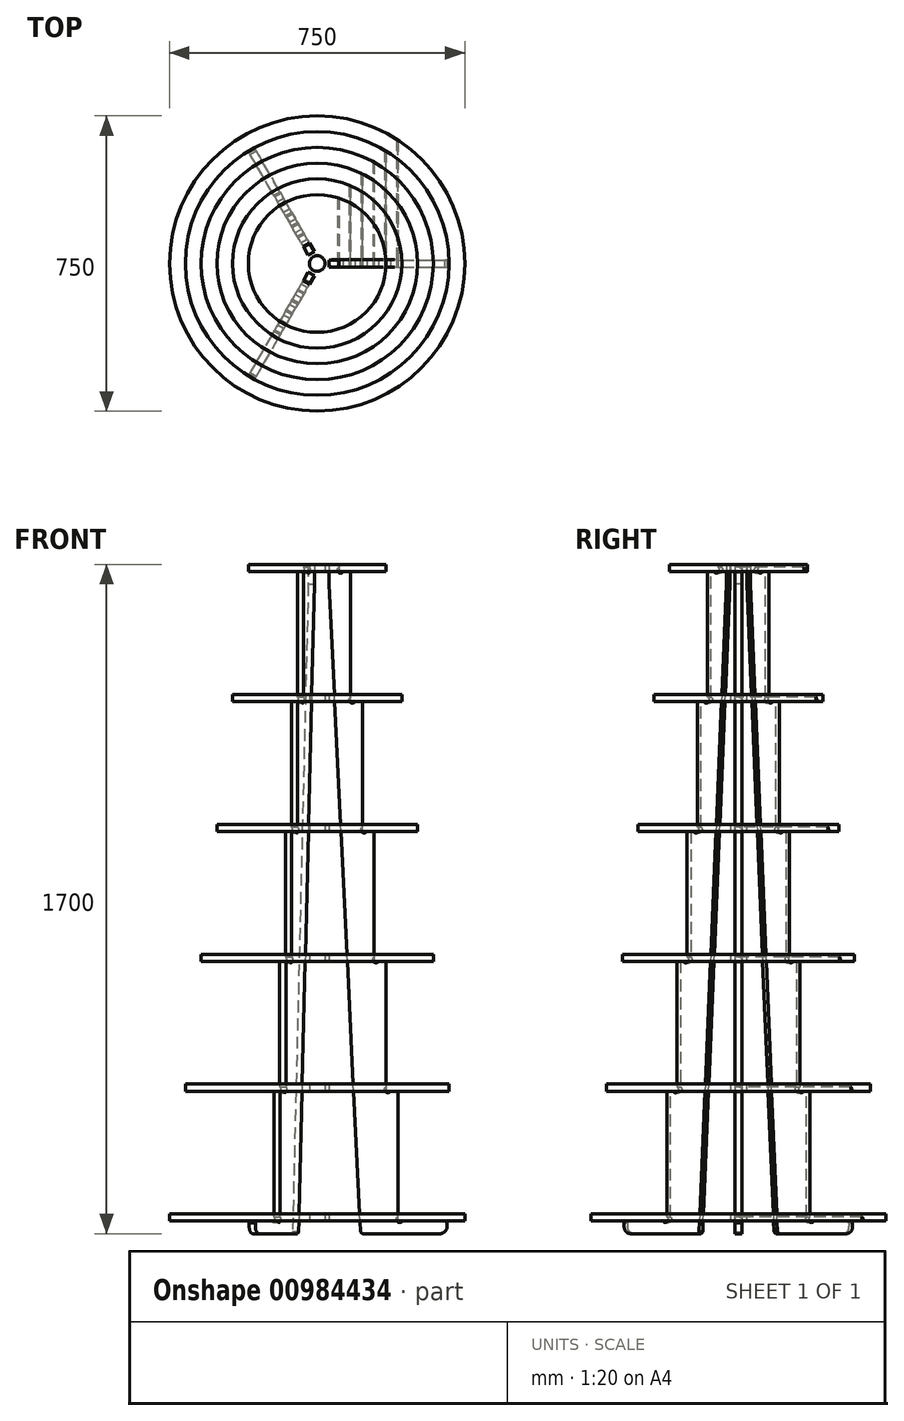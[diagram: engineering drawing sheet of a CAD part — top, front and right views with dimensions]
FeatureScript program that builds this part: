
annotation { "Feature Type Name" : "Feature", "Feature Type Description" : "" }
export const myFeature = defineFeature(function(context is Context, id is Id, definition is map)
    precondition{}
    {
        {
            var Q0;
            Q0=qCreatedBy(makeId("Top.planeOp"),FACE);
            cPlane(context, id + "F0", {"entities" : qUnion([Q0]), "cplaneType" : CPlaneType.OFFSET, "offset" : 50 * mm, "width" : 150 * mm, "height" : 150 * mm});
        }
        {
            var Q0;
            Q0=qCreatedBy(makeId("Top.planeOp"),FACE);
            cPlane(context, id + "F1", {"entities" : qUnion([Q0]), "cplaneType" : CPlaneType.OFFSET, "offset" : 1700 * mm, "width" : 150 * mm, "height" : 150 * mm});
        }
        {
            var Q0;
            Q0=qCreatedBy(id+"F0.planeOp",FACE);
            cPlane(context, id + "F2", {"entities" : qUnion([Q0]), "cplaneType" : CPlaneType.OFFSET, "offset" : (1650 / 5) * mm, "width" : 150 * mm, "height" : 150 * mm});
        }
        {
            var Q0;
            Q0=qCreatedBy(id+"F2.planeOp",FACE);
            cPlane(context, id + "F3", {"entities" : qUnion([Q0]), "cplaneType" : CPlaneType.OFFSET, "offset" : (1650 / 5) * mm, "width" : 150 * mm, "height" : 150 * mm});
        }
        {
            var Q0;
            Q0=qCreatedBy(id+"F3.planeOp",FACE);
            cPlane(context, id + "F4", {"entities" : qUnion([Q0]), "cplaneType" : CPlaneType.OFFSET, "offset" : (1650 / 5) * mm, "width" : 150 * mm, "height" : 150 * mm});
        }
        {
            var Q0;
            Q0=qCreatedBy(id+"F4.planeOp",FACE);
            cPlane(context, id + "F5", {"entities" : qUnion([Q0]), "cplaneType" : CPlaneType.OFFSET, "offset" : (1650 / 5) * mm, "width" : 150 * mm, "height" : 150 * mm});
        }
        {
            var Q0;
            Q0=qCreatedBy(id+"F0.planeOp",FACE);
            var sketch = newSketch(context, id + "F6", { "sketchPlane" : qUnion([Q0])});
            skCircle(sketch, "E0", {"center": v(0, 0) * mm, "radius": 375 * mm});
            skSolve(sketch);
        }
        {
            var Q0;
            Q0=qCreatedBy(id+"F1.planeOp",FACE);
            var sketch = newSketch(context, id + "F7", { "sketchPlane" : qUnion([Q0])});
            skCircle(sketch, "E1", {"center": v(0, 0) * mm, "radius": 175 * mm});
            skSolve(sketch);
        }
        {
            var Q0;
            Q0=qCreatedBy(makeId("Front.planeOp"),FACE);
            var sketch = newSketch(context, id + "F8", { "sketchPlane" : qUnion([Q0])});
            skLineSegment(sketch, "E2", {"start": v(375, 50) * mm, "end": v(175, 1700) * mm, "construction": true});
            skLineSegment(sketch, "E3.0", {"start": v(-175, 1700) * mm, "end": v(175, 1700) * mm, "construction": true});
            skLineSegment(sketch, "E4.0", {"start": v(-375, 50) * mm, "end": v(375, 50) * mm, "construction": true});
            skLineSegment(sketch, "E5", {"start": v(0, 380) * mm, "end": v(335, 380) * mm});
            skLineSegment(sketch, "E6", {"start": v(0, 710) * mm, "end": v(295, 710) * mm});
            skLineSegment(sketch, "E7", {"start": v(0, 1040) * mm, "end": v(255, 1040) * mm});
            skLineSegment(sketch, "E8", {"start": v(0, 1370) * mm, "end": v(215, 1370) * mm});
            skSolve(sketch);
        }
        {
            var Q0;
            Q0=qCreatedBy(id+"F2.planeOp",FACE);
            var sketch = newSketch(context, id + "F9", { "sketchPlane" : qUnion([Q0])});
            skCircle(sketch, "E9", {"center": v(0, 0) * mm, "radius": 335 * mm});
            skPoint(sketch, "E10.0", {"position": v(335, 0) * mm});
            skSolve(sketch);
        }
        {
            var Q0;
            Q0=qCreatedBy(id+"F3.planeOp",FACE);
            var sketch = newSketch(context, id + "F10", { "sketchPlane" : qUnion([Q0])});
            skPoint(sketch, "E11.0", {"position": v(295, 0) * mm});
            skCircle(sketch, "E12", {"center": v(0, 0) * mm, "radius": 295 * mm});
            skSolve(sketch);
        }
        {
            var Q0;
            Q0=qCreatedBy(id+"F4.planeOp",FACE);
            var sketch = newSketch(context, id + "F11", { "sketchPlane" : qUnion([Q0])});
            skPoint(sketch, "E13.0", {"position": v(255, 0) * mm});
            skCircle(sketch, "E14", {"center": v(0, 0) * mm, "radius": 255 * mm});
            skSolve(sketch);
        }
        {
            var Q0;
            Q0=qCreatedBy(id+"F5.planeOp",FACE);
            var sketch = newSketch(context, id + "F12", { "sketchPlane" : qUnion([Q0])});
            skPoint(sketch, "E15.0", {"position": v(215, 0) * mm});
            skCircle(sketch, "E16", {"center": v(0, 0) * mm, "radius": 215 * mm});
            skSolve(sketch);
        }
        {
            var Q0;
            Q0=qCreatedBy(makeId("Front.planeOp"),FACE);
            var sketch = newSketch(context, id + "F13", { "sketchPlane" : qUnion([Q0])});
            skLineSegment(sketch, "E17", {"start": v(0, 0) * mm, "end": v(330, 0) * mm});
            skLineSegment(sketch, "E18", {"start": v(205, 32) * mm, "end": v(205, 362) * mm});
            skLineSegment(sketch, "E19", {"start": v(205, 362) * mm, "end": v(175, 362) * mm});
            skLineSegment(sketch, "E20", {"start": v(145, 1022) * mm, "end": v(115, 1022) * mm});
            skLineSegment(sketch, "E21", {"start": v(115, 1022) * mm, "end": v(115, 1352) * mm});
            skLineSegment(sketch, "E22", {"start": v(30, 1700) * mm, "end": v(55, 1700) * mm});
            skLineSegment(sketch, "E23", {"start": v(55, 1700) * mm, "end": v(55, 1682) * mm});
            skLineSegment(sketch, "E24", {"start": v(85, 1352) * mm, "end": v(115, 1352) * mm});
            skLineSegment(sketch, "E25", {"start": v(55, 1682) * mm, "end": v(85, 1682) * mm});
            skLineSegment(sketch, "E26", {"start": v(85, 1352) * mm, "end": v(85, 1682) * mm});
            skLineSegment(sketch, "E27", {"start": v(145, 1022) * mm, "end": v(145, 692) * mm});
            skLineSegment(sketch, "E28", {"start": v(145, 692) * mm, "end": v(175, 692) * mm});
            skLineSegment(sketch, "E29", {"start": v(175, 692) * mm, "end": v(175, 362) * mm});
            skLineSegment(sketch, "E30", {"start": v(205, 32) * mm, "end": v(330, 32) * mm});
            skLineSegment(sketch, "E31", {"start": v(330, 32) * mm, "end": v(330, 0) * mm});
            skPoint(sketch, "E32.orphan", {"position": v(-14.84, 1022) * mm});
            skPoint(sketch, "E33.orphan", {"position": v(30, 0) * mm});
            skLineSegment(sketch, "E34", {"start": v(0, 0) * mm, "end": v(0, 2212.38) * mm, "construction": true});
            skLineSegment(sketch, "E35", {"start": v(30, 1700) * mm, "end": v(30, 0) * mm});
            skSolve(sketch);
        }
        {
            var Q0;
            Q0=makeQuery(id+"F7.imprint","IMPRINT",FACE,{"disambiguationData":[TD([[makeQuery(id+"F7.imprint","IMPRINT",EDGE,{"derivedFrom":sQuery(id+"F7.wireOp",EDGE,"E1")}),1.0]])]});
            var Q1;
            Q1=makeQuery(id+"F12.imprint","IMPRINT",FACE,{"disambiguationData":[TD([[makeQuery(id+"F12.imprint","IMPRINT",EDGE,{"derivedFrom":sQuery(id+"F12.wireOp",EDGE,"E16")}),1.0]])]});
            var Q2;
            Q2=makeQuery(id+"F11.imprint","IMPRINT",FACE,{"disambiguationData":[TD([[makeQuery(id+"F11.imprint","IMPRINT",EDGE,{"derivedFrom":sQuery(id+"F11.wireOp",EDGE,"E14")}),1.0]])]});
            var Q3;
            Q3=makeQuery(id+"F10.imprint","IMPRINT",FACE,{"disambiguationData":[TD([[makeQuery(id+"F10.imprint","IMPRINT",EDGE,{"derivedFrom":sQuery(id+"F10.wireOp",EDGE,"E12")}),1.0]])]});
            var Q4;
            Q4=makeQuery(id+"F9.imprint","IMPRINT",FACE,{"disambiguationData":[TD([[makeQuery(id+"F9.imprint","IMPRINT",EDGE,{"derivedFrom":sQuery(id+"F9.wireOp",EDGE,"E9")}),1.0]])]});
            var Q5;
            Q5=makeQuery(id+"F6.imprint","IMPRINT",FACE,{"disambiguationData":[TD([[makeQuery(id+"F6.imprint","IMPRINT",EDGE,{"derivedFrom":sQuery(id+"F6.wireOp",EDGE,"E0")}),1.0]])]});
            extrude(context, id + "F14", {"entities" : qUnion([Q0, Q1, Q2, Q3, Q4, Q5]), "oppositeDirection" : true, "depth" : 18 * mm, "offsetDistance" : 25 * mm});
        }
        {
            var Q0;
            Q0=makeQuery(id+"F13.imprint","IMPRINT",FACE,{"disambiguationData":[TD([[makeQuery(id+"F13.imprint","IMPRINT",EDGE,{"derivedFrom":sQuery(id+"F13.wireOp",EDGE,"E18")}),1.0]])]});
            extrude(context, id + "F15", {"entities" : qUnion([Q0]), "operationType" : NewBodyOperationType.REMOVE, "endBound" : BoundingType.SYMMETRIC, "depth" : 18.5 * mm, "offsetDistance" : 25 * mm});
        }
        {
            var Q0;
            Q0=makeQuery(id+"F13.imprint","IMPRINT",FACE,{"disambiguationData":[TD([[makeQuery(id+"F13.imprint","IMPRINT",EDGE,{"derivedFrom":sQuery(id+"F13.wireOp",EDGE,"E18")}),1.0]])]});
            extrude(context, id + "F16", {"entities" : qUnion([Q0]), "endBound" : BoundingType.SYMMETRIC, "depth" : 18 * mm, "offsetDistance" : 25 * mm});
        }
        {
            var Q0;
            Q0=makeQuery(id+"F16.opExtrude","SWEPT_EDGE",EDGE,{"disambiguationData":[OSD([sQuery(id+"F13.wireOp",EDGE,"E17"),sQuery(id+"F13.wireOp",EDGE,"E35")])]});
            chamfer(context, id + "F17", {"entities" : qUnion([Q0]), "chamferType" : ChamferType.TWO_OFFSETS, "width1" : 80 * mm, "oppositeDirection" : false, "width2" : 1650 * mm, "tangentPropagation" : true});
        }
        {
            var Q0;
            Q0=makeQuery(id+"F16.opExtrude","CAP_FACE",FACE,{"disambiguationData":[OSD([sQuery(id+"F13.wireOp",EDGE,"E17"),sQuery(id+"F13.wireOp",EDGE,"E18"),sQuery(id+"F13.wireOp",EDGE,"E19"),sQuery(id+"F13.wireOp",EDGE,"E20"),sQuery(id+"F13.wireOp",EDGE,"E21"),sQuery(id+"F13.wireOp",EDGE,"E22"),sQuery(id+"F13.wireOp",EDGE,"E23"),sQuery(id+"F13.wireOp",EDGE,"E24"),sQuery(id+"F13.wireOp",EDGE,"E25"),sQuery(id+"F13.wireOp",EDGE,"E26"),sQuery(id+"F13.wireOp",EDGE,"E27"),sQuery(id+"F13.wireOp",EDGE,"E28"),sQuery(id+"F13.wireOp",EDGE,"E29"),sQuery(id+"F13.wireOp",EDGE,"E30"),sQuery(id+"F13.wireOp",EDGE,"E31"),sQuery(id+"F13.wireOp",EDGE,"E35")])],"isStart":false});
            var sketch = newSketch(context, id + "F18", { "sketchPlane" : qUnion([Q0])});
            skArc(sketch, "E36", {"start": v(85, 1363.17) * mm, "mid": v(83.59, 1350.59) * mm, "end": v(96.17, 1352) * mm});
            skLineSegment(sketch, "E37", {"start": v(89.31, 1356.31) * mm, "end": v(85, 1352) * mm, "construction": true});
            skLineSegment(sketch, "E38", {"start": v(85, 1352) * mm, "end": v(85, 1363.17) * mm});
            skLineSegment(sketch, "E39", {"start": v(85, 1352) * mm, "end": v(96.17, 1352) * mm});
            skLineSegment(sketch, "E40", {"start": v(85, 1352) * mm, "end": v(83.59, 1350.59) * mm, "construction": true});
            skArc(sketch, "E41", {"start": v(145, 703.17) * mm, "mid": v(143.59, 690.59) * mm, "end": v(156.17, 692) * mm});
            skLineSegment(sketch, "E42", {"start": v(149.31, 696.31) * mm, "end": v(145, 692) * mm, "construction": true});
            skLineSegment(sketch, "E43", {"start": v(145, 692) * mm, "end": v(145, 703.17) * mm});
            skLineSegment(sketch, "E44", {"start": v(145, 692) * mm, "end": v(156.17, 692) * mm});
            skLineSegment(sketch, "E45", {"start": v(145, 692) * mm, "end": v(143.59, 690.59) * mm, "construction": true});
            skArc(sketch, "E46", {"start": v(205, 43.17) * mm, "mid": v(203.59, 30.59) * mm, "end": v(216.17, 32) * mm});
            skLineSegment(sketch, "E47", {"start": v(209.31, 36.31) * mm, "end": v(205, 32) * mm, "construction": true});
            skLineSegment(sketch, "E48", {"start": v(205, 32) * mm, "end": v(205, 43.17) * mm});
            skLineSegment(sketch, "E49", {"start": v(205, 32) * mm, "end": v(216.17, 32) * mm});
            skLineSegment(sketch, "E50", {"start": v(205, 32) * mm, "end": v(203.59, 30.59) * mm, "construction": true});
            skArc(sketch, "E51", {"start": v(175, 373.17) * mm, "mid": v(173.59, 360.59) * mm, "end": v(186.17, 362) * mm});
            skLineSegment(sketch, "E52", {"start": v(179.31, 366.31) * mm, "end": v(175, 362) * mm, "construction": true});
            skLineSegment(sketch, "E53", {"start": v(175, 362) * mm, "end": v(175, 373.17) * mm});
            skLineSegment(sketch, "E54", {"start": v(175, 362) * mm, "end": v(186.17, 362) * mm});
            skLineSegment(sketch, "E55", {"start": v(175, 362) * mm, "end": v(173.59, 360.59) * mm, "construction": true});
            skArc(sketch, "E56", {"start": v(55, 1693.17) * mm, "mid": v(53.59, 1680.59) * mm, "end": v(66.17, 1682) * mm});
            skLineSegment(sketch, "E57", {"start": v(59.31, 1686.31) * mm, "end": v(55, 1682) * mm, "construction": true});
            skLineSegment(sketch, "E58", {"start": v(55, 1682) * mm, "end": v(55, 1693.17) * mm});
            skLineSegment(sketch, "E59", {"start": v(55, 1682) * mm, "end": v(66.17, 1682) * mm});
            skLineSegment(sketch, "E60", {"start": v(55, 1682) * mm, "end": v(53.59, 1680.59) * mm, "construction": true});
            skArc(sketch, "E61", {"start": v(115, 1033.17) * mm, "mid": v(113.59, 1020.59) * mm, "end": v(126.17, 1022) * mm});
            skLineSegment(sketch, "E62", {"start": v(119.31, 1026.31) * mm, "end": v(115, 1022) * mm, "construction": true});
            skLineSegment(sketch, "E63", {"start": v(115, 1022) * mm, "end": v(115, 1033.17) * mm});
            skLineSegment(sketch, "E64", {"start": v(115, 1022) * mm, "end": v(126.17, 1022) * mm});
            skLineSegment(sketch, "E65", {"start": v(115, 1022) * mm, "end": v(113.59, 1020.59) * mm, "construction": true});
            skSolve(sketch);
        }
        {
            var Q0;
            Q0=makeQuery(id+"F18.imprint","IMPRINT",FACE,{"disambiguationData":[TD([[makeQuery(id+"F18.imprint","IMPRINT",EDGE,{"derivedFrom":sQuery(id+"F18.wireOp",EDGE,"E46")}),1.0]])]});
            var Q1;
            Q1=makeQuery(id+"F18.imprint","IMPRINT",FACE,{"disambiguationData":[TD([[makeQuery(id+"F18.imprint","IMPRINT",EDGE,{"derivedFrom":sQuery(id+"F18.wireOp",EDGE,"E51")}),1.0]])]});
            var Q2;
            Q2=makeQuery(id+"F18.imprint","IMPRINT",FACE,{"disambiguationData":[TD([[makeQuery(id+"F18.imprint","IMPRINT",EDGE,{"derivedFrom":sQuery(id+"F18.wireOp",EDGE,"E41")}),1.0]])]});
            var Q3;
            Q3=makeQuery(id+"F18.imprint","IMPRINT",FACE,{"disambiguationData":[TD([[makeQuery(id+"F18.imprint","IMPRINT",EDGE,{"derivedFrom":sQuery(id+"F18.wireOp",EDGE,"E61")}),1.0]])]});
            var Q4;
            Q4=makeQuery(id+"F18.imprint","IMPRINT",FACE,{"disambiguationData":[TD([[makeQuery(id+"F18.imprint","IMPRINT",EDGE,{"derivedFrom":sQuery(id+"F18.wireOp",EDGE,"E36")}),1.0]])]});
            var Q5;
            Q5=makeQuery(id+"F18.imprint","IMPRINT",FACE,{"disambiguationData":[TD([[makeQuery(id+"F18.imprint","IMPRINT",EDGE,{"derivedFrom":sQuery(id+"F18.wireOp",EDGE,"E56")}),1.0]])]});
            extrude(context, id + "F19", {"entities" : qUnion([Q0, Q1, Q2, Q3, Q4, Q5]), "operationType" : NewBodyOperationType.REMOVE, "endBound" : BoundingType.THROUGH_ALL, "oppositeDirection" : true, "depth" : 25 * mm, "offsetDistance" : 25 * mm});
        }
        {
            var Q0;
            Q0=makeQuery(id+"F16.opExtrude","SWEPT_EDGE",EDGE,{"disambiguationData":[OSD([sQuery(id+"F13.wireOp",EDGE,"E17"),sQuery(id+"F13.wireOp",EDGE,"E31")])]});
            fillet(context, id + "F20", {"entities" : qUnion([Q0]), "radius" : 18 * mm, "tangentPropagation" : true, "allowEdgeOverflow" : false});
        }
        {
            var Q0;
            Q0=makeQuery(id+"F16.opExtrude","SWEPT_EDGE",EDGE,{"disambiguationData":[OSD([sQuery(id+"F13.wireOp",EDGE,"E30"),sQuery(id+"F13.wireOp",EDGE,"E31")])]});
            var Q1;
            {var subQ0=sQuery(id+"F13.wireOp",EDGE,"E17");Q1=makeQuery(id+"F17.opChamfer","BLEND_EDGE",EDGE,{"blendedFrom":[makeQuery(id+"F16.opExtrude","SWEPT_EDGE",EDGE,{"disambiguationData":[OSD([subQ0,sQuery(id+"F13.wireOp",EDGE,"E35")])]}),makeQuery(id+"F16.opExtrude","SWEPT_FACE",FACE,{"disambiguationData":[OSD([subQ0])]})],"blendedInto":[makeQuery(id+"F16.opExtrude","SWEPT_FACE",FACE,{"disambiguationData":[OSD([subQ0])]})]});}
            chamfer(context, id + "F21", {"entities" : qUnion([Q0, Q1]), "width" : 5 * mm, "tangentPropagation" : true});
        }
        {
            var Q0;
            Q0=makeQuery(id+"F16.opExtrude","SWEPT_BODY",BODY,{"disambiguationData":[OSD([sQuery(id+"F13.wireOp",EDGE,"E17"),sQuery(id+"F13.wireOp",EDGE,"E18"),sQuery(id+"F13.wireOp",EDGE,"E19"),sQuery(id+"F13.wireOp",EDGE,"E20"),sQuery(id+"F13.wireOp",EDGE,"E21"),sQuery(id+"F13.wireOp",EDGE,"E22"),sQuery(id+"F13.wireOp",EDGE,"E23"),sQuery(id+"F13.wireOp",EDGE,"E24"),sQuery(id+"F13.wireOp",EDGE,"E25"),sQuery(id+"F13.wireOp",EDGE,"E26"),sQuery(id+"F13.wireOp",EDGE,"E27"),sQuery(id+"F13.wireOp",EDGE,"E28"),sQuery(id+"F13.wireOp",EDGE,"E29"),sQuery(id+"F13.wireOp",EDGE,"E30"),sQuery(id+"F13.wireOp",EDGE,"E31"),sQuery(id+"F13.wireOp",EDGE,"E35")])]});
            var Q1;
            Q1=sQuery(id+"F13.wireOp",EDGE,"E34");
            circularPattern(context, id + "F22", {"entities" : qUnion([Q0]), "axis" : qUnion([Q1]), "angle" : 360 * degree, "instanceCount" : 3, "equalSpace" : true});
        }
        {
            var Q0;
            Q0=makeQuery(id+"F14.opExtrude","CAP_FACE",FACE,{"disambiguationData":[OSD([sQuery(id+"F6.wireOp",EDGE,"E0")])],"isStart":false});
            var sketch = newSketch(context, id + "F23", { "sketchPlane" : qUnion([Q0])});
            skCircle(sketch, "E66", {"center": v(0, 0) * mm, "radius": 20 * mm});
            skSolve(sketch);
        }
        {
            var Q0;
            Q0 = qSketchRegion(id + "F23", true);
            extrude(context, id + "F24", {"entities" : qUnion([Q0]), "operationType" : NewBodyOperationType.REMOVE, "endBound" : BoundingType.THROUGH_ALL, "oppositeDirection" : true, "depth" : 25 * mm, "offsetDistance" : 25 * mm});
        }
        {
            var Q0;
            Q0=makeQuery(id+"F4L6b2pkVkDBWmi_6.1.F15.boolean.opBoolean","COPY",EDGE,{"derivedFrom":makeQuery(id+"F4L6b2pkVkDBWmi_6.1.F15.opExtrude","CAP_EDGE",EDGE,{"disambiguationData":[OSD([sQuery(id+"F13.wireOp",EDGE,"E23")])],"isStart":true})});
            var Q1;
            Q1=makeQuery(id+"F4L6b2pkVkDBWmi_6.1.F15.boolean.opBoolean","COPY",EDGE,{"derivedFrom":makeQuery(id+"F4L6b2pkVkDBWmi_6.1.F15.opExtrude","CAP_EDGE",EDGE,{"disambiguationData":[OSD([sQuery(id+"F13.wireOp",EDGE,"E23")])],"isStart":false})});
            var Q2;
            {var subQ0=sQuery(id+"F7.wireOp",EDGE,"E1");var subQ1=sQuery(id+"F13.wireOp",EDGE,"E35");Q2=makeQuery(id+"F4L6b2pkVkDBWmi_6.1.F15.boolean.opBoolean","COPY",EDGE,{"disambiguationData":[TD([makeQuery(id+"F14.opExtrude","CAP_FACE",FACE,{"disambiguationData":[OSD([subQ0])],"isStart":true})])],"derivedFrom":makeQuery(id+"F4L6b2pkVkDBWmi_6.1.F15.opExtrude","CAP_EDGE",EDGE,{"disambiguationData":[OSD([subQ1])],"isStart":false})});}
            var Q3;
            {var subQ0=sQuery(id+"F7.wireOp",EDGE,"E1");var subQ1=sQuery(id+"F13.wireOp",EDGE,"E35");Q3=makeQuery(id+"F4L6b2pkVkDBWmi_6.1.F15.boolean.opBoolean","COPY",EDGE,{"disambiguationData":[TD([makeQuery(id+"F14.opExtrude","CAP_FACE",FACE,{"disambiguationData":[OSD([subQ0])],"isStart":true})])],"derivedFrom":makeQuery(id+"F4L6b2pkVkDBWmi_6.1.F15.opExtrude","CAP_EDGE",EDGE,{"disambiguationData":[OSD([subQ1])],"isStart":true})});}
            var Q4;
            Q4=makeQuery(id+"F4L6b2pkVkDBWmi_6.2.F15.boolean.opBoolean","COPY",EDGE,{"derivedFrom":makeQuery(id+"F4L6b2pkVkDBWmi_6.2.F15.opExtrude","CAP_EDGE",EDGE,{"disambiguationData":[OSD([sQuery(id+"F13.wireOp",EDGE,"E23")])],"isStart":true})});
            var Q5;
            Q5=makeQuery(id+"F15.boolean.opBoolean","COPY",EDGE,{"derivedFrom":makeQuery(id+"F15.opExtrude","CAP_EDGE",EDGE,{"disambiguationData":[OSD([sQuery(id+"F13.wireOp",EDGE,"E23")])],"isStart":false})});
            var Q6;
            Q6=makeQuery(id+"F15.boolean.opBoolean","COPY",EDGE,{"derivedFrom":makeQuery(id+"F15.opExtrude","CAP_EDGE",EDGE,{"disambiguationData":[OSD([sQuery(id+"F13.wireOp",EDGE,"E23")])],"isStart":true})});
            var Q7;
            {var subQ0=sQuery(id+"F7.wireOp",EDGE,"E1");var subQ1=sQuery(id+"F13.wireOp",EDGE,"E35");Q7=makeQuery(id+"F4L6b2pkVkDBWmi_6.2.F15.boolean.opBoolean","COPY",EDGE,{"disambiguationData":[TD([makeQuery(id+"F14.opExtrude","CAP_FACE",FACE,{"disambiguationData":[OSD([subQ0])],"isStart":true})])],"derivedFrom":makeQuery(id+"F4L6b2pkVkDBWmi_6.2.F15.opExtrude","CAP_EDGE",EDGE,{"disambiguationData":[OSD([subQ1])],"isStart":true})});}
            var Q8;
            {var subQ0=sQuery(id+"F7.wireOp",EDGE,"E1");var subQ1=sQuery(id+"F13.wireOp",EDGE,"E35");Q8=makeQuery(id+"F15.boolean.opBoolean","COPY",EDGE,{"disambiguationData":[TD([makeQuery(id+"F14.opExtrude","CAP_FACE",FACE,{"disambiguationData":[OSD([subQ0])],"isStart":true})])],"derivedFrom":makeQuery(id+"F15.opExtrude","CAP_EDGE",EDGE,{"disambiguationData":[OSD([subQ1])],"isStart":true})});}
            var Q9;
            {var subQ0=sQuery(id+"F7.wireOp",EDGE,"E1");var subQ1=sQuery(id+"F13.wireOp",EDGE,"E35");Q9=makeQuery(id+"F4L6b2pkVkDBWmi_6.2.F15.boolean.opBoolean","COPY",EDGE,{"disambiguationData":[TD([makeQuery(id+"F14.opExtrude","CAP_FACE",FACE,{"disambiguationData":[OSD([subQ0])],"isStart":true})])],"derivedFrom":makeQuery(id+"F4L6b2pkVkDBWmi_6.2.F15.opExtrude","CAP_EDGE",EDGE,{"disambiguationData":[OSD([subQ1])],"isStart":false})});}
            var Q10;
            {var subQ0=sQuery(id+"F7.wireOp",EDGE,"E1");var subQ1=sQuery(id+"F13.wireOp",EDGE,"E35");Q10=makeQuery(id+"F15.boolean.opBoolean","COPY",EDGE,{"disambiguationData":[TD([makeQuery(id+"F14.opExtrude","CAP_FACE",FACE,{"disambiguationData":[OSD([subQ0])],"isStart":true})])],"derivedFrom":makeQuery(id+"F15.opExtrude","CAP_EDGE",EDGE,{"disambiguationData":[OSD([subQ1])],"isStart":false})});}
            var Q11;
            Q11=makeQuery(id+"F4L6b2pkVkDBWmi_6.2.F15.boolean.opBoolean","COPY",EDGE,{"derivedFrom":makeQuery(id+"F4L6b2pkVkDBWmi_6.2.F15.opExtrude","CAP_EDGE",EDGE,{"disambiguationData":[OSD([sQuery(id+"F13.wireOp",EDGE,"E23")])],"isStart":false})});
            var Q12;
            Q12=makeQuery(id+"F4L6b2pkVkDBWmi_6.1.F15.boolean.opBoolean","COPY",EDGE,{"derivedFrom":makeQuery(id+"F4L6b2pkVkDBWmi_6.1.F15.opExtrude","CAP_EDGE",EDGE,{"disambiguationData":[OSD([sQuery(id+"F13.wireOp",EDGE,"E26")])],"isStart":false})});
            var Q13;
            {var subQ0=sQuery(id+"F12.wireOp",EDGE,"E16");var subQ1=sQuery(id+"F13.wireOp",EDGE,"E35");Q13=makeQuery(id+"F15.boolean.opBoolean","COPY",EDGE,{"disambiguationData":[TD([makeQuery(id+"F14.opExtrude","CAP_FACE",FACE,{"disambiguationData":[OSD([subQ0])],"isStart":true})])],"derivedFrom":makeQuery(id+"F15.opExtrude","CAP_EDGE",EDGE,{"disambiguationData":[OSD([subQ1])],"isStart":true})});}
            var Q14;
            {var subQ0=sQuery(id+"F12.wireOp",EDGE,"E16");var subQ1=sQuery(id+"F13.wireOp",EDGE,"E35");Q14=makeQuery(id+"F4L6b2pkVkDBWmi_6.2.F15.boolean.opBoolean","COPY",EDGE,{"disambiguationData":[TD([makeQuery(id+"F14.opExtrude","CAP_FACE",FACE,{"disambiguationData":[OSD([subQ0])],"isStart":true})])],"derivedFrom":makeQuery(id+"F4L6b2pkVkDBWmi_6.2.F15.opExtrude","CAP_EDGE",EDGE,{"disambiguationData":[OSD([subQ1])],"isStart":false})});}
            var Q15;
            Q15=makeQuery(id+"F4L6b2pkVkDBWmi_6.1.F15.boolean.opBoolean","COPY",EDGE,{"derivedFrom":makeQuery(id+"F4L6b2pkVkDBWmi_6.1.F15.opExtrude","CAP_EDGE",EDGE,{"disambiguationData":[OSD([sQuery(id+"F13.wireOp",EDGE,"E26")])],"isStart":true})});
            var Q16;
            Q16=makeQuery(id+"F4L6b2pkVkDBWmi_6.2.F15.boolean.opBoolean","COPY",EDGE,{"derivedFrom":makeQuery(id+"F4L6b2pkVkDBWmi_6.2.F15.opExtrude","CAP_EDGE",EDGE,{"disambiguationData":[OSD([sQuery(id+"F13.wireOp",EDGE,"E26")])],"isStart":false})});
            var Q17;
            {var subQ0=sQuery(id+"F12.wireOp",EDGE,"E16");var subQ1=sQuery(id+"F13.wireOp",EDGE,"E35");Q17=makeQuery(id+"F15.boolean.opBoolean","COPY",EDGE,{"disambiguationData":[TD([makeQuery(id+"F14.opExtrude","CAP_FACE",FACE,{"disambiguationData":[OSD([subQ0])],"isStart":true})])],"derivedFrom":makeQuery(id+"F15.opExtrude","CAP_EDGE",EDGE,{"disambiguationData":[OSD([subQ1])],"isStart":false})});}
            var Q18;
            {var subQ0=sQuery(id+"F12.wireOp",EDGE,"E16");var subQ1=sQuery(id+"F13.wireOp",EDGE,"E35");Q18=makeQuery(id+"F4L6b2pkVkDBWmi_6.1.F15.boolean.opBoolean","COPY",EDGE,{"disambiguationData":[TD([makeQuery(id+"F14.opExtrude","CAP_FACE",FACE,{"disambiguationData":[OSD([subQ0])],"isStart":true})])],"derivedFrom":makeQuery(id+"F4L6b2pkVkDBWmi_6.1.F15.opExtrude","CAP_EDGE",EDGE,{"disambiguationData":[OSD([subQ1])],"isStart":true})});}
            var Q19;
            Q19=makeQuery(id+"F4L6b2pkVkDBWmi_6.2.F15.boolean.opBoolean","COPY",EDGE,{"derivedFrom":makeQuery(id+"F4L6b2pkVkDBWmi_6.2.F15.opExtrude","CAP_EDGE",EDGE,{"disambiguationData":[OSD([sQuery(id+"F13.wireOp",EDGE,"E26")])],"isStart":true})});
            var Q20;
            Q20=makeQuery(id+"F15.boolean.opBoolean","COPY",EDGE,{"derivedFrom":makeQuery(id+"F15.opExtrude","CAP_EDGE",EDGE,{"disambiguationData":[OSD([sQuery(id+"F13.wireOp",EDGE,"E26")])],"isStart":false})});
            var Q21;
            {var subQ0=sQuery(id+"F12.wireOp",EDGE,"E16");var subQ1=sQuery(id+"F13.wireOp",EDGE,"E35");Q21=makeQuery(id+"F4L6b2pkVkDBWmi_6.2.F15.boolean.opBoolean","COPY",EDGE,{"disambiguationData":[TD([makeQuery(id+"F14.opExtrude","CAP_FACE",FACE,{"disambiguationData":[OSD([subQ0])],"isStart":true})])],"derivedFrom":makeQuery(id+"F4L6b2pkVkDBWmi_6.2.F15.opExtrude","CAP_EDGE",EDGE,{"disambiguationData":[OSD([subQ1])],"isStart":true})});}
            var Q22;
            {var subQ0=sQuery(id+"F12.wireOp",EDGE,"E16");var subQ1=sQuery(id+"F13.wireOp",EDGE,"E35");Q22=makeQuery(id+"F4L6b2pkVkDBWmi_6.1.F15.boolean.opBoolean","COPY",EDGE,{"disambiguationData":[TD([makeQuery(id+"F14.opExtrude","CAP_FACE",FACE,{"disambiguationData":[OSD([subQ0])],"isStart":true})])],"derivedFrom":makeQuery(id+"F4L6b2pkVkDBWmi_6.1.F15.opExtrude","CAP_EDGE",EDGE,{"disambiguationData":[OSD([subQ1])],"isStart":false})});}
            var Q23;
            Q23=makeQuery(id+"F15.boolean.opBoolean","COPY",EDGE,{"derivedFrom":makeQuery(id+"F15.opExtrude","CAP_EDGE",EDGE,{"disambiguationData":[OSD([sQuery(id+"F13.wireOp",EDGE,"E26")])],"isStart":true})});
            var Q24;
            Q24=makeQuery(id+"F15.boolean.opBoolean","COPY",EDGE,{"derivedFrom":makeQuery(id+"F15.opExtrude","CAP_EDGE",EDGE,{"disambiguationData":[OSD([sQuery(id+"F13.wireOp",EDGE,"E21")])],"isStart":true})});
            var Q25;
            {var subQ0=sQuery(id+"F11.wireOp",EDGE,"E14");var subQ1=sQuery(id+"F13.wireOp",EDGE,"E35");Q25=makeQuery(id+"F4L6b2pkVkDBWmi_6.2.F15.boolean.opBoolean","COPY",EDGE,{"disambiguationData":[TD([makeQuery(id+"F14.opExtrude","CAP_FACE",FACE,{"disambiguationData":[OSD([subQ0])],"isStart":true})])],"derivedFrom":makeQuery(id+"F4L6b2pkVkDBWmi_6.2.F15.opExtrude","CAP_EDGE",EDGE,{"disambiguationData":[OSD([subQ1])],"isStart":true})});}
            var Q26;
            {var subQ0=sQuery(id+"F11.wireOp",EDGE,"E14");var subQ1=sQuery(id+"F13.wireOp",EDGE,"E35");Q26=makeQuery(id+"F4L6b2pkVkDBWmi_6.1.F15.boolean.opBoolean","COPY",EDGE,{"disambiguationData":[TD([makeQuery(id+"F14.opExtrude","CAP_FACE",FACE,{"disambiguationData":[OSD([subQ0])],"isStart":true})])],"derivedFrom":makeQuery(id+"F4L6b2pkVkDBWmi_6.1.F15.opExtrude","CAP_EDGE",EDGE,{"disambiguationData":[OSD([subQ1])],"isStart":false})});}
            var Q27;
            {var subQ0=sQuery(id+"F11.wireOp",EDGE,"E14");var subQ1=sQuery(id+"F13.wireOp",EDGE,"E35");Q27=makeQuery(id+"F15.boolean.opBoolean","COPY",EDGE,{"disambiguationData":[TD([makeQuery(id+"F14.opExtrude","CAP_FACE",FACE,{"disambiguationData":[OSD([subQ0])],"isStart":true})])],"derivedFrom":makeQuery(id+"F15.opExtrude","CAP_EDGE",EDGE,{"disambiguationData":[OSD([subQ1])],"isStart":true})});}
            var Q28;
            Q28=makeQuery(id+"F4L6b2pkVkDBWmi_6.1.F15.boolean.opBoolean","COPY",EDGE,{"derivedFrom":makeQuery(id+"F4L6b2pkVkDBWmi_6.1.F15.opExtrude","CAP_EDGE",EDGE,{"disambiguationData":[OSD([sQuery(id+"F13.wireOp",EDGE,"E21")])],"isStart":false})});
            var Q29;
            {var subQ0=sQuery(id+"F11.wireOp",EDGE,"E14");var subQ1=sQuery(id+"F13.wireOp",EDGE,"E35");Q29=makeQuery(id+"F4L6b2pkVkDBWmi_6.2.F15.boolean.opBoolean","COPY",EDGE,{"disambiguationData":[TD([makeQuery(id+"F14.opExtrude","CAP_FACE",FACE,{"disambiguationData":[OSD([subQ0])],"isStart":true})])],"derivedFrom":makeQuery(id+"F4L6b2pkVkDBWmi_6.2.F15.opExtrude","CAP_EDGE",EDGE,{"disambiguationData":[OSD([subQ1])],"isStart":false})});}
            var Q30;
            Q30=makeQuery(id+"F4L6b2pkVkDBWmi_6.1.F15.boolean.opBoolean","COPY",EDGE,{"derivedFrom":makeQuery(id+"F4L6b2pkVkDBWmi_6.1.F15.opExtrude","CAP_EDGE",EDGE,{"disambiguationData":[OSD([sQuery(id+"F13.wireOp",EDGE,"E21")])],"isStart":true})});
            var Q31;
            Q31=makeQuery(id+"F4L6b2pkVkDBWmi_6.2.F15.boolean.opBoolean","COPY",EDGE,{"derivedFrom":makeQuery(id+"F4L6b2pkVkDBWmi_6.2.F15.opExtrude","CAP_EDGE",EDGE,{"disambiguationData":[OSD([sQuery(id+"F13.wireOp",EDGE,"E21")])],"isStart":false})});
            var Q32;
            {var subQ0=sQuery(id+"F11.wireOp",EDGE,"E14");var subQ1=sQuery(id+"F13.wireOp",EDGE,"E35");Q32=makeQuery(id+"F15.boolean.opBoolean","COPY",EDGE,{"disambiguationData":[TD([makeQuery(id+"F14.opExtrude","CAP_FACE",FACE,{"disambiguationData":[OSD([subQ0])],"isStart":true})])],"derivedFrom":makeQuery(id+"F15.opExtrude","CAP_EDGE",EDGE,{"disambiguationData":[OSD([subQ1])],"isStart":false})});}
            var Q33;
            {var subQ0=sQuery(id+"F11.wireOp",EDGE,"E14");var subQ1=sQuery(id+"F13.wireOp",EDGE,"E35");Q33=makeQuery(id+"F4L6b2pkVkDBWmi_6.1.F15.boolean.opBoolean","COPY",EDGE,{"disambiguationData":[TD([makeQuery(id+"F14.opExtrude","CAP_FACE",FACE,{"disambiguationData":[OSD([subQ0])],"isStart":true})])],"derivedFrom":makeQuery(id+"F4L6b2pkVkDBWmi_6.1.F15.opExtrude","CAP_EDGE",EDGE,{"disambiguationData":[OSD([subQ1])],"isStart":true})});}
            var Q34;
            Q34=makeQuery(id+"F4L6b2pkVkDBWmi_6.2.F15.boolean.opBoolean","COPY",EDGE,{"derivedFrom":makeQuery(id+"F4L6b2pkVkDBWmi_6.2.F15.opExtrude","CAP_EDGE",EDGE,{"disambiguationData":[OSD([sQuery(id+"F13.wireOp",EDGE,"E21")])],"isStart":true})});
            var Q35;
            Q35=makeQuery(id+"F15.boolean.opBoolean","COPY",EDGE,{"derivedFrom":makeQuery(id+"F15.opExtrude","CAP_EDGE",EDGE,{"disambiguationData":[OSD([sQuery(id+"F13.wireOp",EDGE,"E21")])],"isStart":false})});
            var Q36;
            Q36=makeQuery(id+"F15.boolean.opBoolean","COPY",EDGE,{"derivedFrom":makeQuery(id+"F15.opExtrude","CAP_EDGE",EDGE,{"disambiguationData":[OSD([sQuery(id+"F13.wireOp",EDGE,"E27")])],"isStart":false})});
            var Q37;
            {var subQ0=sQuery(id+"F10.wireOp",EDGE,"E12");var subQ1=sQuery(id+"F13.wireOp",EDGE,"E35");Q37=makeQuery(id+"F4L6b2pkVkDBWmi_6.1.F15.boolean.opBoolean","COPY",EDGE,{"disambiguationData":[TD([makeQuery(id+"F14.opExtrude","CAP_FACE",FACE,{"disambiguationData":[OSD([subQ0])],"isStart":true})])],"derivedFrom":makeQuery(id+"F4L6b2pkVkDBWmi_6.1.F15.opExtrude","CAP_EDGE",EDGE,{"disambiguationData":[OSD([subQ1])],"isStart":false})});}
            var Q38;
            {var subQ0=sQuery(id+"F10.wireOp",EDGE,"E12");var subQ1=sQuery(id+"F13.wireOp",EDGE,"E35");Q38=makeQuery(id+"F4L6b2pkVkDBWmi_6.2.F15.boolean.opBoolean","COPY",EDGE,{"disambiguationData":[TD([makeQuery(id+"F14.opExtrude","CAP_FACE",FACE,{"disambiguationData":[OSD([subQ0])],"isStart":true})])],"derivedFrom":makeQuery(id+"F4L6b2pkVkDBWmi_6.2.F15.opExtrude","CAP_EDGE",EDGE,{"disambiguationData":[OSD([subQ1])],"isStart":true})});}
            var Q39;
            Q39=makeQuery(id+"F15.boolean.opBoolean","COPY",EDGE,{"derivedFrom":makeQuery(id+"F15.opExtrude","CAP_EDGE",EDGE,{"disambiguationData":[OSD([sQuery(id+"F13.wireOp",EDGE,"E27")])],"isStart":true})});
            var Q40;
            Q40=makeQuery(id+"F4L6b2pkVkDBWmi_6.1.F15.boolean.opBoolean","COPY",EDGE,{"derivedFrom":makeQuery(id+"F4L6b2pkVkDBWmi_6.1.F15.opExtrude","CAP_EDGE",EDGE,{"disambiguationData":[OSD([sQuery(id+"F13.wireOp",EDGE,"E27")])],"isStart":false})});
            var Q41;
            {var subQ0=sQuery(id+"F10.wireOp",EDGE,"E12");var subQ1=sQuery(id+"F13.wireOp",EDGE,"E35");Q41=makeQuery(id+"F4L6b2pkVkDBWmi_6.2.F15.boolean.opBoolean","COPY",EDGE,{"disambiguationData":[TD([makeQuery(id+"F14.opExtrude","CAP_FACE",FACE,{"disambiguationData":[OSD([subQ0])],"isStart":true})])],"derivedFrom":makeQuery(id+"F4L6b2pkVkDBWmi_6.2.F15.opExtrude","CAP_EDGE",EDGE,{"disambiguationData":[OSD([subQ1])],"isStart":false})});}
            var Q42;
            {var subQ0=sQuery(id+"F10.wireOp",EDGE,"E12");var subQ1=sQuery(id+"F13.wireOp",EDGE,"E35");Q42=makeQuery(id+"F15.boolean.opBoolean","COPY",EDGE,{"disambiguationData":[TD([makeQuery(id+"F14.opExtrude","CAP_FACE",FACE,{"disambiguationData":[OSD([subQ0])],"isStart":true})])],"derivedFrom":makeQuery(id+"F15.opExtrude","CAP_EDGE",EDGE,{"disambiguationData":[OSD([subQ1])],"isStart":true})});}
            var Q43;
            Q43=makeQuery(id+"F4L6b2pkVkDBWmi_6.1.F15.boolean.opBoolean","COPY",EDGE,{"derivedFrom":makeQuery(id+"F4L6b2pkVkDBWmi_6.1.F15.opExtrude","CAP_EDGE",EDGE,{"disambiguationData":[OSD([sQuery(id+"F13.wireOp",EDGE,"E27")])],"isStart":true})});
            var Q44;
            Q44=makeQuery(id+"F4L6b2pkVkDBWmi_6.2.F15.boolean.opBoolean","COPY",EDGE,{"derivedFrom":makeQuery(id+"F4L6b2pkVkDBWmi_6.2.F15.opExtrude","CAP_EDGE",EDGE,{"disambiguationData":[OSD([sQuery(id+"F13.wireOp",EDGE,"E27")])],"isStart":false})});
            var Q45;
            {var subQ0=sQuery(id+"F10.wireOp",EDGE,"E12");var subQ1=sQuery(id+"F13.wireOp",EDGE,"E35");Q45=makeQuery(id+"F15.boolean.opBoolean","COPY",EDGE,{"disambiguationData":[TD([makeQuery(id+"F14.opExtrude","CAP_FACE",FACE,{"disambiguationData":[OSD([subQ0])],"isStart":true})])],"derivedFrom":makeQuery(id+"F15.opExtrude","CAP_EDGE",EDGE,{"disambiguationData":[OSD([subQ1])],"isStart":false})});}
            var Q46;
            {var subQ0=sQuery(id+"F10.wireOp",EDGE,"E12");var subQ1=sQuery(id+"F13.wireOp",EDGE,"E35");Q46=makeQuery(id+"F4L6b2pkVkDBWmi_6.1.F15.boolean.opBoolean","COPY",EDGE,{"disambiguationData":[TD([makeQuery(id+"F14.opExtrude","CAP_FACE",FACE,{"disambiguationData":[OSD([subQ0])],"isStart":true})])],"derivedFrom":makeQuery(id+"F4L6b2pkVkDBWmi_6.1.F15.opExtrude","CAP_EDGE",EDGE,{"disambiguationData":[OSD([subQ1])],"isStart":true})});}
            var Q47;
            Q47=makeQuery(id+"F4L6b2pkVkDBWmi_6.2.F15.boolean.opBoolean","COPY",EDGE,{"derivedFrom":makeQuery(id+"F4L6b2pkVkDBWmi_6.2.F15.opExtrude","CAP_EDGE",EDGE,{"disambiguationData":[OSD([sQuery(id+"F13.wireOp",EDGE,"E27")])],"isStart":true})});
            var Q48;
            Q48=makeQuery(id+"F4L6b2pkVkDBWmi_6.2.F15.boolean.opBoolean","COPY",EDGE,{"derivedFrom":makeQuery(id+"F4L6b2pkVkDBWmi_6.2.F15.opExtrude","CAP_EDGE",EDGE,{"disambiguationData":[OSD([sQuery(id+"F13.wireOp",EDGE,"E29")])],"isStart":true})});
            var Q49;
            {var subQ0=sQuery(id+"F9.wireOp",EDGE,"E9");var subQ1=sQuery(id+"F13.wireOp",EDGE,"E35");Q49=makeQuery(id+"F4L6b2pkVkDBWmi_6.1.F15.boolean.opBoolean","COPY",EDGE,{"disambiguationData":[TD([makeQuery(id+"F14.opExtrude","CAP_FACE",FACE,{"disambiguationData":[OSD([subQ0])],"isStart":true})])],"derivedFrom":makeQuery(id+"F4L6b2pkVkDBWmi_6.1.F15.opExtrude","CAP_EDGE",EDGE,{"disambiguationData":[OSD([subQ1])],"isStart":true})});}
            var Q50;
            Q50=makeQuery(id+"F15.boolean.opBoolean","COPY",EDGE,{"derivedFrom":makeQuery(id+"F15.opExtrude","CAP_EDGE",EDGE,{"disambiguationData":[OSD([sQuery(id+"F13.wireOp",EDGE,"E29")])],"isStart":false})});
            var Q51;
            Q51=makeQuery(id+"F15.boolean.opBoolean","COPY",EDGE,{"derivedFrom":makeQuery(id+"F15.opExtrude","CAP_EDGE",EDGE,{"disambiguationData":[OSD([sQuery(id+"F13.wireOp",EDGE,"E29")])],"isStart":true})});
            var Q52;
            {var subQ0=sQuery(id+"F9.wireOp",EDGE,"E9");var subQ1=sQuery(id+"F13.wireOp",EDGE,"E35");Q52=makeQuery(id+"F4L6b2pkVkDBWmi_6.2.F15.boolean.opBoolean","COPY",EDGE,{"disambiguationData":[TD([makeQuery(id+"F14.opExtrude","CAP_FACE",FACE,{"disambiguationData":[OSD([subQ0])],"isStart":true})])],"derivedFrom":makeQuery(id+"F4L6b2pkVkDBWmi_6.2.F15.opExtrude","CAP_EDGE",EDGE,{"disambiguationData":[OSD([subQ1])],"isStart":true})});}
            var Q53;
            {var subQ0=sQuery(id+"F9.wireOp",EDGE,"E9");var subQ1=sQuery(id+"F13.wireOp",EDGE,"E35");Q53=makeQuery(id+"F4L6b2pkVkDBWmi_6.1.F15.boolean.opBoolean","COPY",EDGE,{"disambiguationData":[TD([makeQuery(id+"F14.opExtrude","CAP_FACE",FACE,{"disambiguationData":[OSD([subQ0])],"isStart":true})])],"derivedFrom":makeQuery(id+"F4L6b2pkVkDBWmi_6.1.F15.opExtrude","CAP_EDGE",EDGE,{"disambiguationData":[OSD([subQ1])],"isStart":false})});}
            var Q54;
            {var subQ0=sQuery(id+"F9.wireOp",EDGE,"E9");var subQ1=sQuery(id+"F13.wireOp",EDGE,"E35");Q54=makeQuery(id+"F4L6b2pkVkDBWmi_6.2.F15.boolean.opBoolean","COPY",EDGE,{"disambiguationData":[TD([makeQuery(id+"F14.opExtrude","CAP_FACE",FACE,{"disambiguationData":[OSD([subQ0])],"isStart":true})])],"derivedFrom":makeQuery(id+"F4L6b2pkVkDBWmi_6.2.F15.opExtrude","CAP_EDGE",EDGE,{"disambiguationData":[OSD([subQ1])],"isStart":false})});}
            var Q55;
            Q55=makeQuery(id+"F4L6b2pkVkDBWmi_6.1.F15.boolean.opBoolean","COPY",EDGE,{"derivedFrom":makeQuery(id+"F4L6b2pkVkDBWmi_6.1.F15.opExtrude","CAP_EDGE",EDGE,{"disambiguationData":[OSD([sQuery(id+"F13.wireOp",EDGE,"E29")])],"isStart":false})});
            var Q56;
            {var subQ0=sQuery(id+"F9.wireOp",EDGE,"E9");var subQ1=sQuery(id+"F13.wireOp",EDGE,"E35");Q56=makeQuery(id+"F15.boolean.opBoolean","COPY",EDGE,{"disambiguationData":[TD([makeQuery(id+"F14.opExtrude","CAP_FACE",FACE,{"disambiguationData":[OSD([subQ0])],"isStart":true})])],"derivedFrom":makeQuery(id+"F15.opExtrude","CAP_EDGE",EDGE,{"disambiguationData":[OSD([subQ1])],"isStart":true})});}
            var Q57;
            Q57=makeQuery(id+"F4L6b2pkVkDBWmi_6.1.F15.boolean.opBoolean","COPY",EDGE,{"derivedFrom":makeQuery(id+"F4L6b2pkVkDBWmi_6.1.F15.opExtrude","CAP_EDGE",EDGE,{"disambiguationData":[OSD([sQuery(id+"F13.wireOp",EDGE,"E29")])],"isStart":true})});
            var Q58;
            Q58=makeQuery(id+"F4L6b2pkVkDBWmi_6.2.F15.boolean.opBoolean","COPY",EDGE,{"derivedFrom":makeQuery(id+"F4L6b2pkVkDBWmi_6.2.F15.opExtrude","CAP_EDGE",EDGE,{"disambiguationData":[OSD([sQuery(id+"F13.wireOp",EDGE,"E29")])],"isStart":false})});
            var Q59;
            {var subQ0=sQuery(id+"F9.wireOp",EDGE,"E9");var subQ1=sQuery(id+"F13.wireOp",EDGE,"E35");Q59=makeQuery(id+"F15.boolean.opBoolean","COPY",EDGE,{"disambiguationData":[TD([makeQuery(id+"F14.opExtrude","CAP_FACE",FACE,{"disambiguationData":[OSD([subQ0])],"isStart":true})])],"derivedFrom":makeQuery(id+"F15.opExtrude","CAP_EDGE",EDGE,{"disambiguationData":[OSD([subQ1])],"isStart":false})});}
            var Q60;
            Q60=makeQuery(id+"F4L6b2pkVkDBWmi_6.2.F15.boolean.opBoolean","COPY",EDGE,{"derivedFrom":makeQuery(id+"F4L6b2pkVkDBWmi_6.2.F15.opExtrude","CAP_EDGE",EDGE,{"disambiguationData":[OSD([sQuery(id+"F13.wireOp",EDGE,"E18")])],"isStart":false})});
            var Q61;
            Q61=makeQuery(id+"F4L6b2pkVkDBWmi_6.1.F15.boolean.opBoolean","COPY",EDGE,{"derivedFrom":makeQuery(id+"F4L6b2pkVkDBWmi_6.1.F15.opExtrude","CAP_EDGE",EDGE,{"disambiguationData":[OSD([sQuery(id+"F13.wireOp",EDGE,"E18")])],"isStart":true})});
            var Q62;
            {var subQ0=sQuery(id+"F6.wireOp",EDGE,"E0");var subQ1=sQuery(id+"F13.wireOp",EDGE,"E35");Q62=makeQuery(id+"F15.boolean.opBoolean","COPY",EDGE,{"disambiguationData":[TD([makeQuery(id+"F14.opExtrude","CAP_FACE",FACE,{"disambiguationData":[OSD([subQ0])],"isStart":true})])],"derivedFrom":makeQuery(id+"F15.opExtrude","CAP_EDGE",EDGE,{"disambiguationData":[OSD([subQ1])],"isStart":false})});}
            var Q63;
            Q63=makeQuery(id+"F4L6b2pkVkDBWmi_6.2.F15.boolean.opBoolean","COPY",EDGE,{"derivedFrom":makeQuery(id+"F4L6b2pkVkDBWmi_6.2.F15.opExtrude","CAP_EDGE",EDGE,{"disambiguationData":[OSD([sQuery(id+"F13.wireOp",EDGE,"E18")])],"isStart":true})});
            var Q64;
            {var subQ0=sQuery(id+"F6.wireOp",EDGE,"E0");var subQ1=sQuery(id+"F13.wireOp",EDGE,"E35");Q64=makeQuery(id+"F4L6b2pkVkDBWmi_6.1.F15.boolean.opBoolean","COPY",EDGE,{"disambiguationData":[TD([makeQuery(id+"F14.opExtrude","CAP_FACE",FACE,{"disambiguationData":[OSD([subQ0])],"isStart":true})])],"derivedFrom":makeQuery(id+"F4L6b2pkVkDBWmi_6.1.F15.opExtrude","CAP_EDGE",EDGE,{"disambiguationData":[OSD([subQ1])],"isStart":true})});}
            var Q65;
            Q65=makeQuery(id+"F15.boolean.opBoolean","COPY",EDGE,{"derivedFrom":makeQuery(id+"F15.opExtrude","CAP_EDGE",EDGE,{"disambiguationData":[OSD([sQuery(id+"F13.wireOp",EDGE,"E18")])],"isStart":false})});
            var Q66;
            {var subQ0=sQuery(id+"F6.wireOp",EDGE,"E0");var subQ1=sQuery(id+"F13.wireOp",EDGE,"E35");Q66=makeQuery(id+"F4L6b2pkVkDBWmi_6.1.F15.boolean.opBoolean","COPY",EDGE,{"disambiguationData":[TD([makeQuery(id+"F14.opExtrude","CAP_FACE",FACE,{"disambiguationData":[OSD([subQ0])],"isStart":true})])],"derivedFrom":makeQuery(id+"F4L6b2pkVkDBWmi_6.1.F15.opExtrude","CAP_EDGE",EDGE,{"disambiguationData":[OSD([subQ1])],"isStart":false})});}
            var Q67;
            {var subQ0=sQuery(id+"F6.wireOp",EDGE,"E0");var subQ1=sQuery(id+"F13.wireOp",EDGE,"E35");Q67=makeQuery(id+"F4L6b2pkVkDBWmi_6.2.F15.boolean.opBoolean","COPY",EDGE,{"disambiguationData":[TD([makeQuery(id+"F14.opExtrude","CAP_FACE",FACE,{"disambiguationData":[OSD([subQ0])],"isStart":true})])],"derivedFrom":makeQuery(id+"F4L6b2pkVkDBWmi_6.2.F15.opExtrude","CAP_EDGE",EDGE,{"disambiguationData":[OSD([subQ1])],"isStart":true})});}
            var Q68;
            Q68=makeQuery(id+"F15.boolean.opBoolean","COPY",EDGE,{"derivedFrom":makeQuery(id+"F15.opExtrude","CAP_EDGE",EDGE,{"disambiguationData":[OSD([sQuery(id+"F13.wireOp",EDGE,"E18")])],"isStart":true})});
            var Q69;
            Q69=makeQuery(id+"F4L6b2pkVkDBWmi_6.1.F15.boolean.opBoolean","COPY",EDGE,{"derivedFrom":makeQuery(id+"F4L6b2pkVkDBWmi_6.1.F15.opExtrude","CAP_EDGE",EDGE,{"disambiguationData":[OSD([sQuery(id+"F13.wireOp",EDGE,"E18")])],"isStart":false})});
            var Q70;
            {var subQ0=sQuery(id+"F6.wireOp",EDGE,"E0");var subQ1=sQuery(id+"F13.wireOp",EDGE,"E35");Q70=makeQuery(id+"F15.boolean.opBoolean","COPY",EDGE,{"disambiguationData":[TD([makeQuery(id+"F14.opExtrude","CAP_FACE",FACE,{"disambiguationData":[OSD([subQ0])],"isStart":true})])],"derivedFrom":makeQuery(id+"F15.opExtrude","CAP_EDGE",EDGE,{"disambiguationData":[OSD([subQ1])],"isStart":true})});}
            var Q71;
            {var subQ0=sQuery(id+"F6.wireOp",EDGE,"E0");var subQ1=sQuery(id+"F13.wireOp",EDGE,"E35");Q71=makeQuery(id+"F4L6b2pkVkDBWmi_6.2.F15.boolean.opBoolean","COPY",EDGE,{"disambiguationData":[TD([makeQuery(id+"F14.opExtrude","CAP_FACE",FACE,{"disambiguationData":[OSD([subQ0])],"isStart":true})])],"derivedFrom":makeQuery(id+"F4L6b2pkVkDBWmi_6.2.F15.opExtrude","CAP_EDGE",EDGE,{"disambiguationData":[OSD([subQ1])],"isStart":false})});}
            fillet(context, id + "F25", {"entities" : qUnion([Q0, Q1, Q2, Q3, Q4, Q5, Q6, Q7, Q8, Q9, Q10, Q11, Q12, Q13, Q14, Q15, Q16, Q17, Q18, Q19, Q20, Q21, Q22, Q23, Q24, Q25, Q26, Q27, Q28, Q29, Q30, Q31, Q32, Q33, Q34, Q35, Q36, Q37, Q38, Q39, Q40, Q41, Q42, Q43, Q44, Q45, Q46, Q47, Q48, Q49, Q50, Q51, Q52, Q53, Q54, Q55, Q56, Q57, Q58, Q59, Q60, Q61, Q62, Q63, Q64, Q65, Q66, Q67, Q68, Q69, Q70, Q71]), "radius" : 8.2 * mm, "tangentPropagation" : true, "allowEdgeOverflow" : false});
        }
    });
